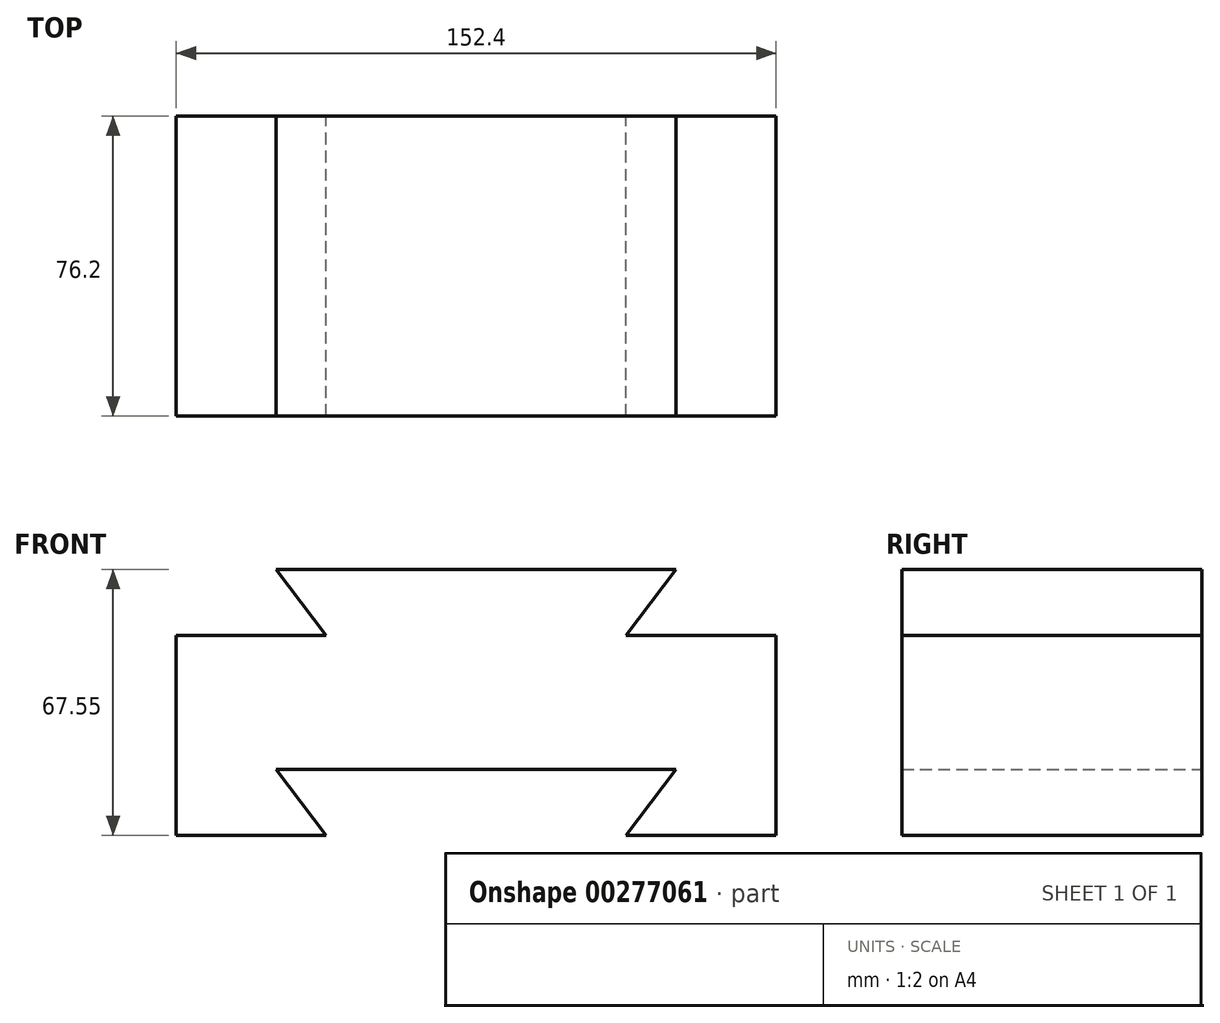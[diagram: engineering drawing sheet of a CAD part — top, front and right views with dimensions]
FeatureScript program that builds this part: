
annotation { "Feature Type Name" : "Feature", "Feature Type Description" : "" }
export const myFeature = defineFeature(function(context is Context, id is Id, definition is map)
    precondition{}
    {
        {
            var Q0;
            Q0=qCreatedBy(makeId("Front.planeOp"),FACE);
            var sketch = newSketch(context, id + "F0", { "sketchPlane" : qUnion([Q0])});
            skLineSegment(sketch, "E0.bottom", {"start": v(-76.2, 25.4) * mm, "end": v(76.2, 25.4) * mm});
            skLineSegment(sketch, "E0.top", {"start": v(-76.2, -25.4) * mm, "end": v(-38.1, -25.4) * mm});
            skLineSegment(sketch, "E0.left", {"start": v(-76.2, 25.4) * mm, "end": v(-76.2, -25.4) * mm});
            skLineSegment(sketch, "E0.right", {"start": v(76.2, 25.4) * mm, "end": v(76.2, -25.4) * mm});
            skPoint(sketch, "E0.middle", {"position": v(0, 0) * mm});
            skPoint(sketch, "E1", {"position": v(0, 25.4) * mm});
            skLineSegment(sketch, "E2", {"start": v(-38.1, 25.4) * mm, "end": v(38.1, 25.4) * mm});
            skLineSegment(sketch, "E3", {"start": v(-38.1, 25.4) * mm, "end": v(-50.8, 42.15) * mm});
            skLineSegment(sketch, "E4", {"start": v(-50.8, 42.15) * mm, "end": v(50.8, 42.15) * mm});
            skLineSegment(sketch, "E5", {"start": v(50.8, 42.15) * mm, "end": v(38.1, 25.4) * mm});
            skPoint(sketch, "E6", {"position": v(0, 42.15) * mm});
            skPoint(sketch, "E7", {"position": v(0, -25.4) * mm});
            skLineSegment(sketch, "E8", {"start": v(38.1, -25.4) * mm, "end": v(50.8, -8.64) * mm});
            skLineSegment(sketch, "E9", {"start": v(50.8, -8.64) * mm, "end": v(-50.8, -8.64) * mm});
            skLineSegment(sketch, "E10", {"start": v(-50.8, -8.64) * mm, "end": v(-38.1, -25.4) * mm});
            skLineSegment(sketch, "E11.trimOffspring", {"start": v(38.1, -25.4) * mm, "end": v(76.2, -25.4) * mm});
            skSolve(sketch);
        }
        {
            var Q0;
            Q0 = qSketchRegion(id + "F0", true);
            extrude(context, id + "F1", {"entities" : qUnion([Q0]), "depth" : 76.2 * mm});
        }
    });
